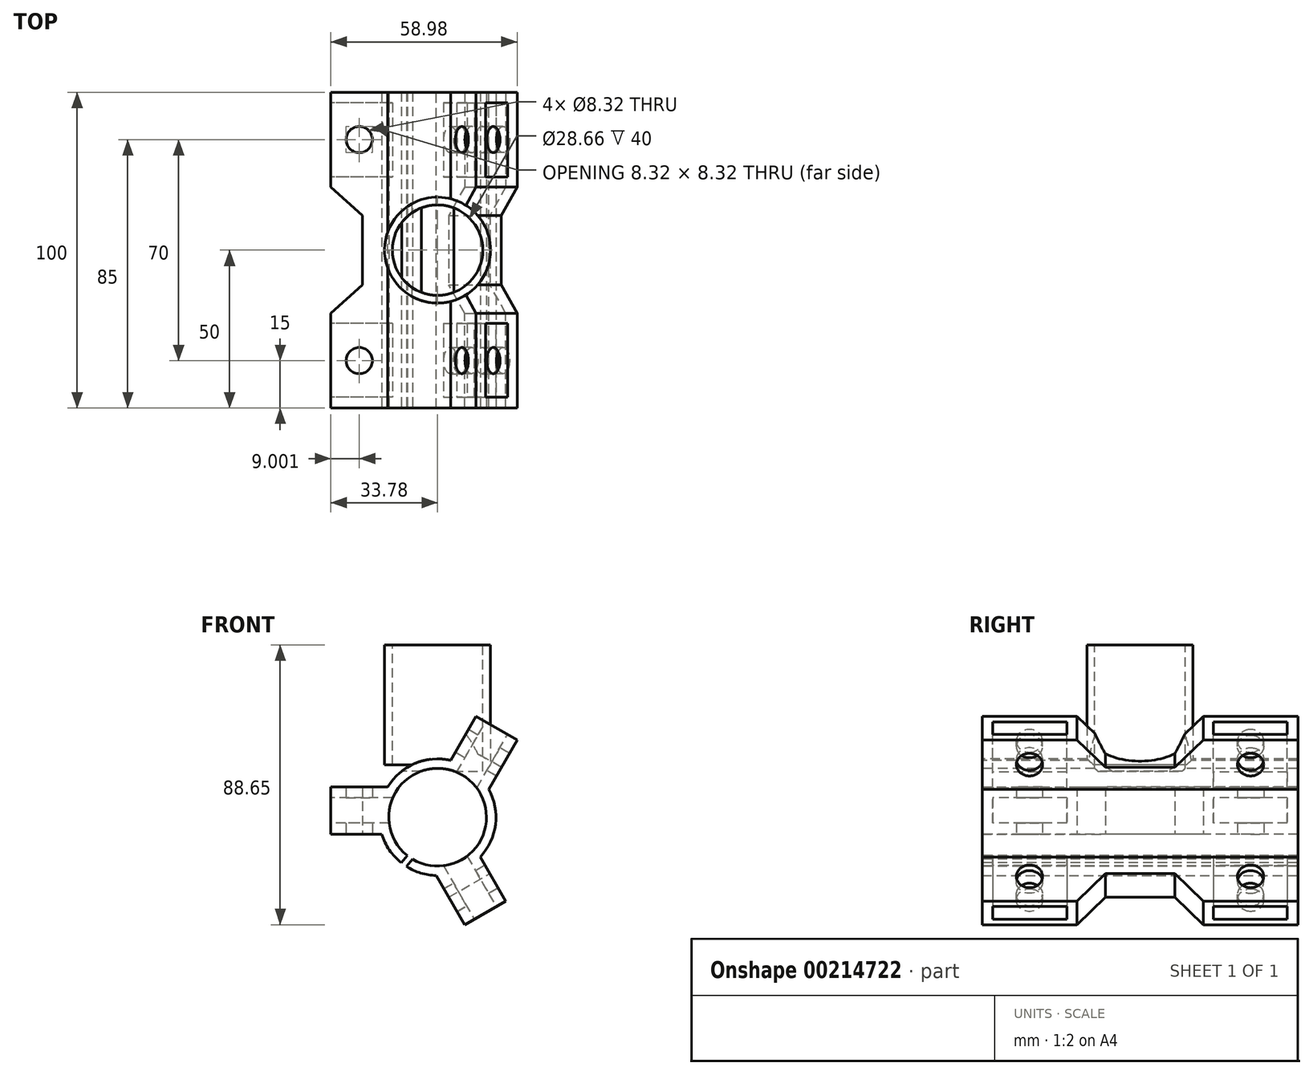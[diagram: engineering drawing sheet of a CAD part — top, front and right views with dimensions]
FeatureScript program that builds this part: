
annotation { "Feature Type Name" : "Feature", "Feature Type Description" : "" }
export const myFeature = defineFeature(function(context is Context, id is Id, definition is map)
    precondition{}
    {
        {
            var Q0;
            Q0=qCreatedBy(makeId("Top.planeOp"),FACE);
            var sketch = newSketch(context, id + "F0", { "sketchPlane" : qUnion([Q0])});
            skLineSegment(sketch, "E0", {"start": v(0, 0) * mm, "end": v(-13.78, 0) * mm, "construction": true});
            skLineSegment(sketch, "E1", {"start": v(-13.78, 0) * mm, "end": v(-13.78, 50) * mm, "construction": true});
            skLineSegment(sketch, "E2", {"start": v(-15.78, 0) * mm, "end": v(-15.78, 50) * mm});
            skLineSegment(sketch, "E3", {"start": v(-15.78, 0) * mm, "end": v(-33.78, 0) * mm});
            skLineSegment(sketch, "E4", {"start": v(-33.78, 0) * mm, "end": v(-33.78, 30) * mm});
            skLineSegment(sketch, "E5", {"start": v(-33.78, 30) * mm, "end": v(-15.78, 0) * mm, "construction": true});
            skLineSegment(sketch, "E6", {"start": v(-33.78, 0) * mm, "end": v(-15.78, 30) * mm, "construction": true});
            skCircle(sketch, "E7", {"center": v(-24.78, 15) * mm, "radius": 11 * mm, "construction": true});
            skCircle(sketch, "E8", {"center": v(-24.78, 15) * mm, "radius": 4.16 * mm});
            skLineSegment(sketch, "E9", {"start": v(-15.78, 39) * mm, "end": v(-23.75, 39) * mm, "construction": true});
            skLineSegment(sketch, "E10", {"start": v(-33.78, 30) * mm, "end": v(-23.75, 39) * mm});
            skLineSegment(sketch, "E11", {"start": v(-23.75, 39) * mm, "end": v(-23.75, 50) * mm});
            skLineSegment(sketch, "E12", {"start": v(-15.78, 50) * mm, "end": v(-23.75, 50) * mm, "construction": true});
            skLineSegment(sketch, "E13.MirrorCS", {"start": v(-23.75, 61) * mm, "end": v(-23.75, 50) * mm});
            skLineSegment(sketch, "E14.MirrorCS", {"start": v(-33.78, 70) * mm, "end": v(-23.75, 61) * mm});
            skLineSegment(sketch, "E15.MirrorCS", {"start": v(-33.78, 100) * mm, "end": v(-33.78, 70) * mm});
            skLineSegment(sketch, "E16.MirrorCS", {"start": v(-15.78, 100) * mm, "end": v(-33.78, 100) * mm});
            skLineSegment(sketch, "E17.MirrorCS", {"start": v(-15.78, 100) * mm, "end": v(-15.78, 50) * mm});
            skCircle(sketch, "E18.MirrorC", {"center": v(-24.78, 85) * mm, "radius": 4.16 * mm});
            skLineSegment(sketch, "E19.MirrorCS", {"start": v(-13.78, 100) * mm, "end": v(-13.78, 50) * mm, "construction": true});
            skCircle(sketch, "E20.MirrorC", {"center": v(-24.78, 85) * mm, "radius": 11 * mm, "construction": true});
            skSolve(sketch);
        }
        {
            var Q0;
            Q0=makeQuery(id+"F0.imprint","IMPRINT",FACE,{"disambiguationData":[TD([[makeQuery(id+"F0.imprint","IMPRINT",EDGE,{"derivedFrom":sQuery(id+"F0.wireOp",EDGE,"E2")}),1.0]])]});
            extrude(context, id + "F1", {"entities" : qUnion([Q0]), "depth" : 15 * mm});
        }
        {
            var Q0;
            Q0=makeQuery(id+"F1.opExtrude","SWEPT_FACE",FACE,{"disambiguationData":[OSD([sQuery(id+"F0.wireOp",EDGE,"E3")])]});
            var sketch = newSketch(context, id + "F2", { "sketchPlane" : qUnion([Q0])});
            skCircle(sketch, "E21", {"center": v(0, 5.4) * mm, "radius": 18.47 * mm, "construction": true});
            skCircle(sketch, "E22", {"center": v(0, 5.4) * mm, "radius": 15.47 * mm, "construction": true});
            skPoint(sketch, "E23.endSnap0", {"position": v(-15.78, 7.5) * mm});
            skLineSegment(sketch, "E24", {"start": v(0, 5.4) * mm, "end": v(-15.47, 5.4) * mm, "construction": true});
            skLineSegment(sketch, "E25", {"start": v(0, 5.4) * mm, "end": v(-7.73, -8) * mm, "construction": true});
            skLineSegment(sketch, "E26", {"start": v(0, 5.4) * mm, "end": v(-7.73, 18.8) * mm, "construction": true});
            skArc(sketch, "E27", {"start": v(-7.73, 18.8) * mm, "mid": v(-15.47, 5.4) * mm, "end": v(-7.73, -8) * mm});
            skLineSegment(sketch, "E28", {"start": v(-7.73, 18.8) * mm, "end": v(-9.23, 21.4) * mm});
            skLineSegment(sketch, "E29", {"start": v(-7.73, -8) * mm, "end": v(-9.23, -10.6) * mm});
            skCircle(sketch, "E30", {"center": v(0, 5.4) * mm, "radius": 13.78 * mm, "construction": true});
            skLineSegment(sketch, "E31", {"start": v(-15.47, 5.4) * mm, "end": v(-18.47, 5.4) * mm, "construction": true});
            skArc(sketch, "E32", {"start": v(-9.23, 21.4) * mm, "mid": v(-18.47, 5.4) * mm, "end": v(-9.23, -10.6) * mm});
            skSolve(sketch);
        }
        {
            var Q0;
            {var subQ0=sQuery(id+"F2.wireOp",EDGE,"E21");var subQ1=sQuery(id+"F0.wireOp",EDGE,"E3");var subQ2=makeQuery(id+"F1.opExtrude","SWEPT_EDGE",EDGE,{"disambiguationData":[OSD([sQuery(id+"F0.wireOp",EDGE,"E2"),subQ1])]});var subQ3=makeQuery(id+"F2.imprint","INTERSECT",VERTEX,{"derivedFrom":[subQ2,makeQuery(id+"F1.opExtrude","CAP_EDGE",EDGE,{"disambiguationData":[OSD([subQ1])],"isStart":true}),subQ0]});Q0=makeQuery(id+"F2.imprint","IMPRINT",FACE,{"disambiguationData":[TD([[makeQuery(id+"F2.imprint","IMPRINT",EDGE,{"disambiguationData":[TD([[subQ3,1.0]])],"derivedFrom":subQ0}),1.0]])]});}
            var Q1;
            {var subQ0=sQuery(id+"F2.wireOp",EDGE,"g3xJxAlq-R5pZ-Eeo2-CjEf-WmfwMOpCXLWw");Q1=makeQuery(id+"F2.imprint","IMPRINT",FACE,{"disambiguationData":[TD([[makeQuery(id+"F2.imprint","IMPRINT",EDGE,{"derivedFrom":subQ0}),-1.0]])]});}
            var Q2;
            Q2=makeQuery(id+"F2.imprint","IMPRINT",FACE,{"disambiguationData":[TD([[makeQuery(id+"F2.imprint","IMPRINT",EDGE,{"derivedFrom":sQuery(id+"F2.wireOp",EDGE,"E22")}),-1.0]])]});
            var Q3;
            Q3=makeQuery(id+"F2.imprint","IMPRINT",FACE,{"disambiguationData":[TD([[makeQuery(id+"F2.imprint","IMPRINT",EDGE,{"derivedFrom":sQuery(id+"F2.wireOp",EDGE,"E27")}),-1.0]])]});
            extrude(context, id + "F3", {"entities" : qUnion([Q0, Q1, Q2, Q3]), "operationType" : NewBodyOperationType.ADD, "oppositeDirection" : true, "depth" : 100 * mm});
        }
        {
            var Q0;
            Q0=makeQuery(id+"F1.opExtrude","SWEPT_FACE",FACE,{"disambiguationData":[OSD([sQuery(id+"F0.wireOp",EDGE,"E15.MirrorCS")])]});
            var sketch = newSketch(context, id + "F4", { "sketchPlane" : qUnion([Q0])});
            skLineSegment(sketch, "E33.bottom", {"start": v(-96.6, 11.5) * mm, "end": v(-73.2, 11.5) * mm});
            skLineSegment(sketch, "E33.top", {"start": v(-96.6, 3.5) * mm, "end": v(-73.2, 3.5) * mm});
            skLineSegment(sketch, "E33.left", {"start": v(-96.6, 11.5) * mm, "end": v(-96.6, 3.5) * mm});
            skLineSegment(sketch, "E33.right", {"start": v(-73.2, 11.5) * mm, "end": v(-73.2, 3.5) * mm});
            skLineSegment(sketch, "E34.bottom", {"start": v(-3.4, 3.5) * mm, "end": v(-26.8, 3.5) * mm});
            skLineSegment(sketch, "E34.top", {"start": v(-3.4, 11.5) * mm, "end": v(-26.8, 11.5) * mm});
            skLineSegment(sketch, "E34.left", {"start": v(-3.4, 3.5) * mm, "end": v(-3.4, 11.5) * mm});
            skLineSegment(sketch, "E34.right", {"start": v(-26.8, 3.5) * mm, "end": v(-26.8, 11.5) * mm});
            skSolve(sketch);
        }
        {
            var Q0;
            Q0=makeQuery(id+"F4.imprint","IMPRINT",FACE,{"disambiguationData":[TD([[makeQuery(id+"F4.imprint","IMPRINT",EDGE,{"derivedFrom":sQuery(id+"F4.wireOp",EDGE,"E33.bottom")}),-1.0]])]});
            var Q1;
            Q1=makeQuery(id+"F4.imprint","IMPRINT",FACE,{"disambiguationData":[TD([[makeQuery(id+"F4.imprint","IMPRINT",EDGE,{"derivedFrom":sQuery(id+"F4.wireOp",EDGE,"E34.bottom")}),-1.0]])]});
            extrude(context, id + "F5", {"entities" : qUnion([Q0, Q1]), "operationType" : NewBodyOperationType.REMOVE, "oppositeDirection" : true, "depth" : 25 * mm});
        }
        {
            var Q0;
            {var subQ0=sQuery(id+"F0.wireOp",EDGE,"E3");Q0=makeQuery(id+"F3.boolean.opBoolean","MERGE",FACE,{"derivedFrom":[makeQuery(id+"F1.opExtrude","SWEPT_FACE",FACE,{"disambiguationData":[OSD([subQ0])]}),makeQuery(id+"F3.opExtrude","CAP_FACE",FACE,{"disambiguationData":[OSD([sQuery(id+"F0.wireOp",EDGE,"E2"),subQ0,sQuery(id+"F2.wireOp",EDGE,"sGRMKCaJ-qwij-XAyk-PemZ-jGETvxKNh2jk"),sQuery(id+"F2.wireOp",EDGE,"E27"),sQuery(id+"F2.wireOp",EDGE,"E28"),sQuery(id+"F2.wireOp",EDGE,"E29")])],"isStart":true})]});}
            var sketch = newSketch(context, id + "F6", { "sketchPlane" : qUnion([Q0])});
            skCircle(sketch, "E35", {"center": v(0, 5.4) * mm, "radius": 15.47 * mm});
            skSolve(sketch);
        }
        {
            var Q0;
            Q0=makeQuery(id+"F1.opExtrude","SWEPT_BODY",BODY,{"disambiguationData":[OSD([sQuery(id+"F0.wireOp",EDGE,"E2"),sQuery(id+"F0.wireOp",EDGE,"E3"),sQuery(id+"F0.wireOp",EDGE,"E4"),sQuery(id+"F0.wireOp",EDGE,"E8"),sQuery(id+"F0.wireOp",EDGE,"E10"),sQuery(id+"F0.wireOp",EDGE,"E11"),sQuery(id+"F0.wireOp",EDGE,"E13.MirrorCS"),sQuery(id+"F0.wireOp",EDGE,"E14.MirrorCS"),sQuery(id+"F0.wireOp",EDGE,"E15.MirrorCS"),sQuery(id+"F0.wireOp",EDGE,"E16.MirrorCS"),sQuery(id+"F0.wireOp",EDGE,"E17.MirrorCS"),sQuery(id+"F0.wireOp",EDGE,"E18.MirrorC")])]});
            var Q1;
            Q1=sQuery(id+"F6.wireOp",EDGE,"E35");
            circularPattern(context, id + "F7", {"operationType" : NewBodyOperationType.ADD, "entities" : qUnion([Q0]), "axis" : qUnion([Q1]), "angle" : 360 * degree, "instanceCount" : 3, "equalSpace" : true, "computeTransformsWithoutBuiltin" : true});
        }
        {
            var Q0;
            Q0=qCreatedBy(makeId("Top.planeOp"),FACE);
            var sketch = newSketch(context, id + "F8", { "sketchPlane" : qUnion([Q0])});
            skCircle(sketch, "E36", {"center": v(0, 50) * mm, "radius": 13.78 * mm});
            skCircle(sketch, "E37", {"center": v(0, 50) * mm, "radius": 16.78 * mm});
            skSolve(sketch);
        }
        {
            var Q0;
            Q0=makeQuery(id+"F8.imprint","IMPRINT",FACE,{"disambiguationData":[TD([[makeQuery(id+"F8.imprint","IMPRINT",EDGE,{"derivedFrom":sQuery(id+"F8.wireOp",EDGE,"E36")}),-1.0]])]});
            extrude(context, id + "F9", {"entities" : qUnion([Q0]), "operationType" : NewBodyOperationType.ADD, "depth" : 60 * mm, "hasSecondDirection" : true, "secondDirectionOppositeDirection" : false, "secondDirectionDepth" : 22 * mm});
        }
        {
            var Q0;
            Q0=makeQuery(id+"F9.opExtrude","CAP_FACE",FACE,{"disambiguationData":[OSD([sQuery(id+"F8.wireOp",EDGE,"E36"),sQuery(id+"F8.wireOp",EDGE,"E37")])],"isStart":false});
            var sketch = newSketch(context, id + "F10", { "sketchPlane" : qUnion([Q0])});
            skCircle(sketch, "E38", {"center": v(0, 50) * mm, "radius": 13.78 * mm});
            skSolve(sketch);
        }
        {
            var Q0;
            Q0=makeQuery(id+"F10.imprint","IMPRINT",FACE,{"disambiguationData":[TD([[makeQuery(id+"F10.imprint","IMPRINT",EDGE,{"derivedFrom":sQuery(id+"F10.wireOp",EDGE,"E38")}),1.0]])]});
            extrude(context, id + "F11", {"entities" : qUnion([Q0]), "operationType" : NewBodyOperationType.REMOVE, "oppositeDirection" : true, "depth" : 40 * mm});
        }
        {
            var Q0;
            Q0=makeQuery(id+"F9.opExtrude","CAP_FACE",FACE,{"disambiguationData":[OSD([sQuery(id+"F8.wireOp",EDGE,"E36"),sQuery(id+"F8.wireOp",EDGE,"E37")])],"isStart":false});
            var sketch = newSketch(context, id + "F12", { "sketchPlane" : qUnion([Q0])});
            skCircle(sketch, "E39", {"center": v(0, 50) * mm, "radius": 14.33 * mm});
            skSolve(sketch);
        }
        {
            var Q0;
            Q0=makeQuery(id+"F12.imprint","IMPRINT",FACE,{"disambiguationData":[TD([[makeQuery(id+"F12.imprint","IMPRINT",EDGE,{"derivedFrom":sQuery(id+"F12.wireOp",EDGE,"E39")}),1.0]])]});
            extrude(context, id + "F13", {"entities" : qUnion([Q0]), "operationType" : NewBodyOperationType.REMOVE, "oppositeDirection" : true, "depth" : 40 * mm});
        }
        {
            var Q0;
            Q0=qCreatedBy(makeId("Front.planeOp"),FACE);
            var sketch = newSketch(context, id + "F14", { "sketchPlane" : qUnion([Q0])});
            skLineSegment(sketch, "E40", {"start": v(-6.69, -3.04) * mm, "end": v(-13.21, -11.24) * mm});
            skLineSegment(sketch, "E41", {"start": v(-13.21, -11.24) * mm, "end": v(-11.65, -12.48) * mm});
            skLineSegment(sketch, "E42", {"start": v(-11.65, -12.48) * mm, "end": v(-4.92, -4.04) * mm});
            skLineSegment(sketch, "E43", {"start": v(-4.92, -4.04) * mm, "end": v(-6.69, -3.04) * mm});
            skSolve(sketch);
        }
        {
            var Q0;
            Q0=qSketchRegion(id+"F14",true);
            extrude(context, id + "F15", {"entities" : qUnion([Q0]), "operationType" : NewBodyOperationType.REMOVE, "oppositeDirection" : true, "depth" : 100 * mm});
        }
    });
